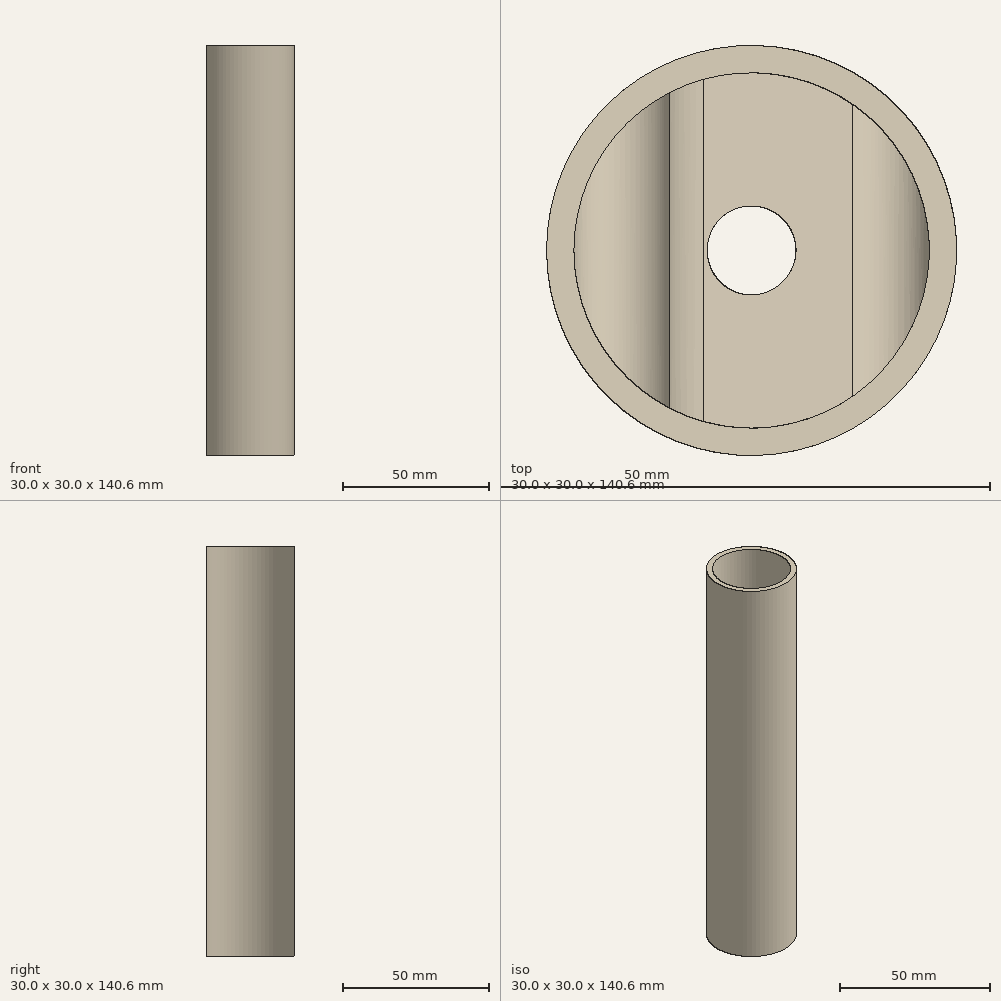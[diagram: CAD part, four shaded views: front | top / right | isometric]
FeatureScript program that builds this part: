
annotation { "Feature Type Name" : "Feature", "Feature Type Description" : "" }
export const myFeature = defineFeature(function(context is Context, id is Id, definition is map)
    precondition{}
    {
        {
            var Q0;
            Q0=qCreatedBy(makeId("Front.planeOp"),FACE);
            var sketch = newSketch(context, id + "F0", { "sketchPlane" : qUnion([Q0])});
            skLineSegment(sketch, "E0.bottom", {"start": v(15, 0) * mm, "end": v(0, 0) * mm, "construction": true});
            skLineSegment(sketch, "E0.top", {"start": v(15, 160) * mm, "end": v(0, 160) * mm, "construction": true});
            skLineSegment(sketch, "E0.left", {"start": v(15, 0) * mm, "end": v(15, 160) * mm, "construction": true});
            skLineSegment(sketch, "E0.right", {"start": v(0, 0) * mm, "end": v(0, 160) * mm, "construction": true});
            skLineSegment(sketch, "E1.MirrorCS", {"start": v(-15, 0) * mm, "end": v(-15, 160) * mm, "construction": true});
            skLineSegment(sketch, "E2", {"start": v(13, 0) * mm, "end": v(13, 160) * mm, "construction": true});
            skLineSegment(sketch, "E3.MirrorCS", {"start": v(-13, 0) * mm, "end": v(-13, 160) * mm, "construction": true});
            skLineSegment(sketch, "E4.MirrorCS", {"start": v(-15, 0) * mm, "end": v(0, 0) * mm, "construction": true});
            skLineSegment(sketch, "E5.MirrorCS", {"start": v(-15, 160) * mm, "end": v(0, 160) * mm, "construction": true});
            skLineSegment(sketch, "E6", {"start": v(3.5, 0) * mm, "end": v(3.5, 160) * mm, "construction": true});
            skLineSegment(sketch, "E7.MirrorCS", {"start": v(-3.5, 0) * mm, "end": v(-3.5, 160) * mm, "construction": true});
            skSolve(sketch);
        }
        {
            var Q0;
            Q0=qCreatedBy(makeId("Front.planeOp"),FACE);
            var sketch = newSketch(context, id + "F1", { "sketchPlane" : qUnion([Q0])});
            skArc(sketch, "E8", {"start": v(-13.08, 33) * mm, "mid": v(-9.35, 29.44) * mm, "end": v(-6, 33.35) * mm});
            skArc(sketch, "E9", {"start": v(-13.08, 23.7) * mm, "mid": v(-10.14, 27.9) * mm, "end": v(-5.15, 26.66) * mm});
            skArc(sketch, "E10", {"start": v(7.37, 17.07) * mm, "mid": v(10.97, 16.65) * mm, "end": v(12.98, 19.67) * mm});
            skArc(sketch, "E11", {"start": v(12.98, 9.26) * mm, "mid": v(11.86, 12.31) * mm, "end": v(8.97, 13.81) * mm});
            skArc(sketch, "E12", {"start": v(8.97, 13.81) * mm, "mid": v(7.8, 14.12) * mm, "end": v(6.74, 14.74) * mm});
            skArc(sketch, "E13", {"start": v(-6, 33.35) * mm, "mid": v(-5.17, 30.52) * mm, "end": v(-3.56, 28.05) * mm});
            skLineSegment(sketch, "E14", {"start": v(-13.08, 33) * mm, "end": v(-13.08, 23.7) * mm});
            skLineSegment(sketch, "E15", {"start": v(-3.56, 28.05) * mm, "end": v(7.37, 17.07) * mm});
            skLineSegment(sketch, "E16", {"start": v(-5.15, 26.66) * mm, "end": v(6.74, 14.74) * mm});
            skLineSegment(sketch, "E17", {"start": v(12.98, 9.26) * mm, "end": v(12.98, 19.67) * mm});
            skArc(sketch, "E18", {"start": v(-13.08, 54.39) * mm, "mid": v(-9.35, 50.84) * mm, "end": v(-6, 54.74) * mm});
            skArc(sketch, "E19", {"start": v(-13.08, 45.09) * mm, "mid": v(-10.14, 49.3) * mm, "end": v(-5.15, 48.06) * mm});
            skArc(sketch, "E20", {"start": v(7.37, 38.46) * mm, "mid": v(10.97, 38.05) * mm, "end": v(12.98, 41.07) * mm});
            skArc(sketch, "E21", {"start": v(12.98, 30.65) * mm, "mid": v(11.86, 33.7) * mm, "end": v(8.97, 35.2) * mm});
            skArc(sketch, "E22", {"start": v(8.97, 35.2) * mm, "mid": v(7.8, 35.52) * mm, "end": v(6.74, 36.14) * mm});
            skArc(sketch, "E23", {"start": v(-6, 54.74) * mm, "mid": v(-5.17, 51.91) * mm, "end": v(-3.56, 49.44) * mm});
            skLineSegment(sketch, "E24", {"start": v(-13.08, 54.39) * mm, "end": v(-13.08, 45.09) * mm});
            skLineSegment(sketch, "E25", {"start": v(-3.56, 49.44) * mm, "end": v(7.37, 38.46) * mm});
            skLineSegment(sketch, "E26", {"start": v(-5.15, 48.06) * mm, "end": v(6.74, 36.14) * mm});
            skLineSegment(sketch, "E27", {"start": v(12.98, 30.65) * mm, "end": v(12.98, 41.07) * mm});
            skArc(sketch, "E28", {"start": v(-13.08, 78.1) * mm, "mid": v(-9.35, 74.56) * mm, "end": v(-6, 78.46) * mm});
            skArc(sketch, "E29", {"start": v(-13.08, 68.8) * mm, "mid": v(-10.14, 73.02) * mm, "end": v(-5.15, 71.78) * mm});
            skArc(sketch, "E30", {"start": v(7.37, 62.18) * mm, "mid": v(10.97, 61.77) * mm, "end": v(12.98, 64.79) * mm});
            skArc(sketch, "E31", {"start": v(12.98, 54.37) * mm, "mid": v(11.86, 57.42) * mm, "end": v(8.97, 58.93) * mm});
            skArc(sketch, "E32", {"start": v(8.97, 58.93) * mm, "mid": v(7.8, 59.24) * mm, "end": v(6.74, 59.86) * mm});
            skArc(sketch, "E33", {"start": v(-6, 78.46) * mm, "mid": v(-5.17, 75.63) * mm, "end": v(-3.56, 73.16) * mm});
            skLineSegment(sketch, "E34", {"start": v(-13.08, 78.1) * mm, "end": v(-13.08, 68.8) * mm});
            skLineSegment(sketch, "E35", {"start": v(-3.56, 73.16) * mm, "end": v(7.37, 62.18) * mm});
            skLineSegment(sketch, "E36", {"start": v(-5.15, 71.78) * mm, "end": v(6.74, 59.86) * mm});
            skLineSegment(sketch, "E37", {"start": v(12.98, 54.37) * mm, "end": v(12.98, 64.79) * mm});
            skArc(sketch, "E38", {"start": v(-13.08, 104.36) * mm, "mid": v(-9.35, 100.8) * mm, "end": v(-6, 104.71) * mm});
            skArc(sketch, "E39", {"start": v(-13.08, 95.06) * mm, "mid": v(-10.14, 99.27) * mm, "end": v(-5.15, 98.03) * mm});
            skArc(sketch, "E40", {"start": v(7.37, 88.43) * mm, "mid": v(10.97, 88.02) * mm, "end": v(12.98, 91.04) * mm});
            skArc(sketch, "E41", {"start": v(12.98, 80.62) * mm, "mid": v(11.86, 83.68) * mm, "end": v(8.97, 85.18) * mm});
            skArc(sketch, "E42", {"start": v(8.97, 85.18) * mm, "mid": v(7.8, 85.49) * mm, "end": v(6.74, 86.1) * mm});
            skArc(sketch, "E43", {"start": v(-6, 104.71) * mm, "mid": v(-5.17, 101.88) * mm, "end": v(-3.56, 99.41) * mm});
            skLineSegment(sketch, "E44", {"start": v(-13.08, 104.36) * mm, "end": v(-13.08, 95.06) * mm});
            skLineSegment(sketch, "E45", {"start": v(-3.56, 99.41) * mm, "end": v(7.37, 88.43) * mm});
            skLineSegment(sketch, "E46", {"start": v(-5.15, 98.03) * mm, "end": v(6.74, 86.1) * mm});
            skLineSegment(sketch, "E47", {"start": v(12.98, 80.62) * mm, "end": v(12.98, 91.04) * mm});
            skSolve(sketch);
        }
        {
            var Q0;
            Q0=qSketchRegion(id+"F1",true);
            extrude(context, id + "F2", {"entities" : qUnion([Q0]), "depth" : 15 * mm, "hasSecondDirection" : true, "secondDirectionOppositeDirection" : true, "secondDirectionDepth" : 15 * mm});
        }
        {
            var Q0;
            Q0=qCreatedBy(makeId("Top.planeOp"),FACE);
            var sketch = newSketch(context, id + "F3", { "sketchPlane" : qUnion([Q0])});
            skCircle(sketch, "E48", {"center": v(0, 0) * mm, "radius": 13 * mm});
            skCircle(sketch, "E49", {"center": v(0, 0) * mm, "radius": 20.3 * mm});
            skSolve(sketch);
        }
        {
            var Q0;
            Q0=makeQuery(id+"F3.imprint","IMPRINT",FACE,{"disambiguationData":[TD([[makeQuery(id+"F3.imprint","IMPRINT",EDGE,{"derivedFrom":sQuery(id+"F3.wireOp",EDGE,"E48")}),-1.0]])]});
            extrude(context, id + "F4", {"entities" : qUnion([Q0]), "operationType" : NewBodyOperationType.REMOVE, "endBound" : BoundingType.THROUGH_ALL, "depth" : 25 * mm});
        }
        {
            var Q0;
            Q0=qCreatedBy(makeId("Front.planeOp"),FACE);
            var sketch = newSketch(context, id + "F5", { "sketchPlane" : qUnion([Q0])});
            skLineSegment(sketch, "E50", {"start": v(0, 3.1) * mm, "end": v(15, 3.1) * mm});
            skArc(sketch, "E51", {"start": v(13, 9.41) * mm, "mid": v(10.05, 5.75) * mm, "end": v(5.38, 6.28) * mm});
            skLineSegment(sketch, "E52", {"start": v(13, 127.81) * mm, "end": v(13, 9.41) * mm});
            skLineSegment(sketch, "E53", {"start": v(13, 143.67) * mm, "end": v(15, 143.67) * mm});
            skLineSegment(sketch, "E54", {"start": v(13, 143.67) * mm, "end": v(13, 127.81) * mm});
            skLineSegment(sketch, "E55", {"start": v(5.38, 6.28) * mm, "end": v(0, 6.28) * mm});
            skLineSegment(sketch, "E56", {"start": v(0, 6.28) * mm, "end": v(0, 3.1) * mm});
            skLineSegment(sketch, "E57", {"start": v(15, 3.1) * mm, "end": v(15, 143.67) * mm});
            skSolve(sketch);
        }
        {
            var Q0;
            Q0=qSketchRegion(id+"F5",true);
            var Q1;
            Q1=sQuery(id+"F0.wireOp",EDGE,"E0.right");
            revolve(context, id + "F6", {"entities" : qUnion([Q0]), "axis" : qUnion([Q1]), "revolveType" : RevolveType.FULL});
        }
        {
            var Q0;
            Q0=qCreatedBy(makeId("Top.planeOp"),FACE);
            var sketch = newSketch(context, id + "F7", { "sketchPlane" : qUnion([Q0])});
            skCircle(sketch, "E58", {"center": v(0, 0) * mm, "radius": 3.25 * mm});
            skSolve(sketch);
        }
        {
            var Q0;
            Q0=qSketchRegion(id+"F7",true);
            var Q1;
            Q1=sQuery(id+"F7.wireOp",EDGE,"E58");
            extrude(context, id + "F8", {"entities" : qUnion([Q0]), "operationType" : NewBodyOperationType.REMOVE, "surfaceEntities" : qUnion([Q1]), "endBound" : BoundingType.THROUGH_ALL, "depth" : 25 * mm, "hasSecondDirection" : true, "secondDirectionOppositeDirection" : true, "secondDirectionDepth" : 25 * mm});
        }
    });
